# Revit family: 2039100(n0300)
name_source: partatom
category: Security Devices
units: mm (PartAtom-declared; Revit-internal decimal feet)

## family parameters
Always vertical = No
Cut with Voids When Loaded = No
Host = Ceiling
OmniClass Number = 23.85.30.14
OmniClass Title = Presence Detection/Registration
Room Calculation Point = No
Shared = Yes

## types (2) — shared parameters
zero-valued in all types: A, EF001992

## per-type parameters (varying)
- Type 1: CTN=0; EF000218=0 mm  [stored 0 ft]; EF000259=0; EF000846=0 mm  [stored 0 ft]; EF001322=0 mm  [stored 0 ft]; EF001323=0 mm  [stored 0 ft]; EF003843=0 mm  [stored 0 ft]; EF003882=0; EF004265=0 mm  [stored 0 ft]; EF006589=0; EF006590=0; EF008011=0 mm  [stored 0 ft]; EF010886=0 mm  [stored 0 ft]; EF010945=0 mm  [stored 0 ft]; EF010946=0 mm  [stored 0 ft]; LOG=0; NOCUPEROU=0; PRICEQUANTITY=0; QUANTITYINT=0; QUANTITYMIN=0
- 2039100: ARTICLENO=NB; BOMINFO=LINA; CATALOG=Theben; COO=HU; CTN=90314990; DEEPLINK_PRODUKTSEITE=http://www.theben.de; DESCLONG=Passive infrared (PIR) presence detector for flush-mounting, flat design, frame in white included, frame in black or silver available as separate accessories, Three channels light for controlling light groups, switching or constant light control, Shortening the overrun time light for short presence, Mixed light measurement, Square 360° detection area, Light switch-off delay self-learning, Stand-by functionality, 2 presence channels with switch-on delay adjustable or inactive, Switch-off delay adjustable, Test functions, Integrated bus coupler and power supply through bus; DESCSHORT=KNX presence detector for ceiling installation, 3 x light and 2 x HVAC, max. 8 x 8 m at height 3.5 m; EF000003=EV000383; EF000007=White; EF000010=Presence detector; EF000139=Untreated; EF000147=false; EF000218=69 mm  [stored 0.226378 ft]; EF000259=5; EF000846=40 mm  [stored 0.131234 ft]; EF001098=true; EF001257=Thermoplast; EF001322=4000 mm  [stored 13.1234 ft]; EF001323=4000 mm  [stored 13.1234 ft]; EF001499=true; EF001500=false; EF001501=false; EF001504=true; EF002169=Plastic; EF003831=false; EF003843=8000 mm; EF003876=true; EF003882=9010; EF003898=true; EF004265=40 mm  [stored 0.131234 ft]; EF004530=false; EF006243=false; EF006311=false; EF006569=matt; EF006582=0, 360 °; EF006589=30; EF006590=60; EF007575=true; EF007667=true; EF008011=3000 mm; EF008855=false; EF009466=false; EF010886=3 mm  [stored 0.00984252 ft]; EF010945=76 mm  [stored 0.249344 ft]; EF010946=40 mm  [stored 0.131234 ft]; EF016048=false; GEBRAUCHSANLEITUNG=http://www.theben.de; INTNO=7612748005839; LINA=2039100; LOG=300; MANUID=2039100; MANUNAME=Theben AG; MANUTYPEDESC=PlanoSpot 360 KNX DE WH; Manufacturer=Theben; Model=2039100; NB=2039100(N0300); NBSYN=$MANUID.($SA.$A.$LOG.); NN=PlanoSpot KNX; NOCUPEROU=1; PRICEQUANTITY=1; PRODUKTDATENBLATT=http://www.theben.de; QUANTITYINT=1; QUANTITYMIN=1; REACH_ERKLAERUNG=http://www.theben.de; REMARKS=ERP-GROUP 360; SA=None; SUPPLIER=THEBEN; SUPPLIERALTNO=2039100

note: [stored X ft] marks values corroborated as IEEE doubles in the binary element streams (Revit-internal decimal feet)

## geometry (parser evidence)
native form markers: Sweep x12
no freeform markers — native parametric forms only
